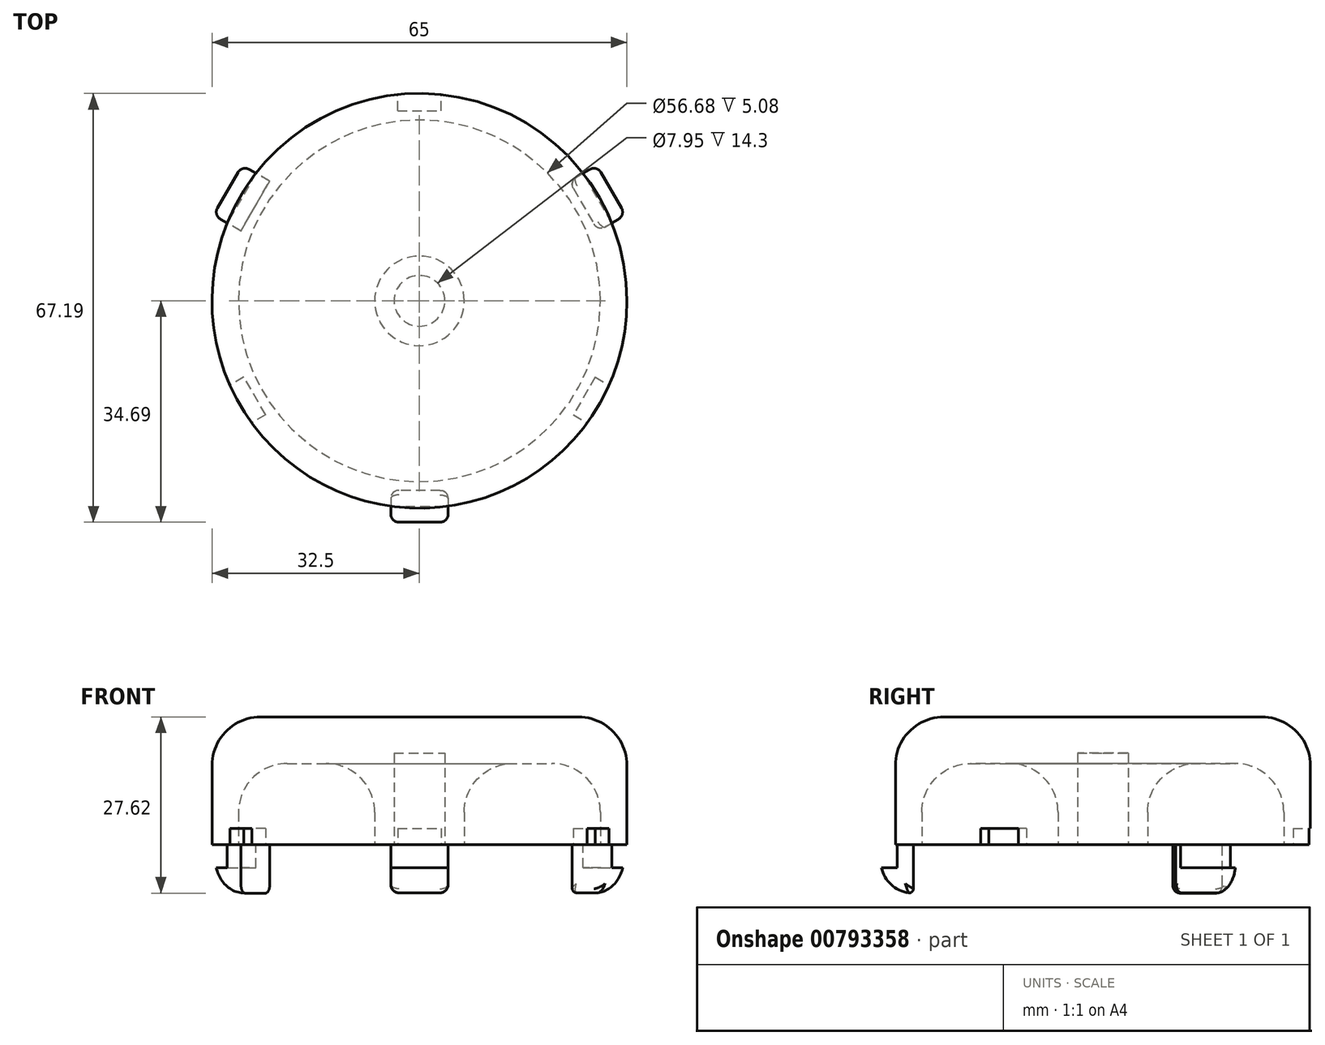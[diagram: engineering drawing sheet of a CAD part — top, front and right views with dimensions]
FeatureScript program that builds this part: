
annotation { "Feature Type Name" : "Feature", "Feature Type Description" : "" }
export const myFeature = defineFeature(function(context is Context, id is Id, definition is map)
    precondition{}
    {
        {
            var Q0;
            Q0=qCreatedBy(makeId("Top.planeOp"),FACE);
            var sketch = newSketch(context, id + "F0", { "sketchPlane" : qUnion([Q0])});
            skCircle(sketch, "E0", {"center": v(0, 0) * mm, "radius": 32.5 * mm});
            skSolve(sketch);
        }
        {
            var Q0;
            Q0=makeQuery(id+"F0.imprint","IMPRINT",FACE,{"disambiguationData":[TD([[makeQuery(id+"F0.imprint","IMPRINT",EDGE,{"derivedFrom":sQuery(id+"F0.wireOp",EDGE,"E0")}),1.0]])]});
            extrude(context, id + "F1", {"entities" : qUnion([Q0]), "depth" : 20 * mm, "offsetDistance" : 25.4 * mm});
        }
        {
            var Q0;
            Q0=makeQuery(id+"F1.opExtrude","CAP_FACE",FACE,{"disambiguationData":[OSD([sQuery(id+"F0.wireOp",EDGE,"E0")])],"isStart":false});
            fillet(context, id + "F2", {"entities" : qUnion([Q0]), "radius" : 7.62 * mm, "tangentPropagation" : true, "allowEdgeOverflow" : false});
        }
        {
            var Q0;
            Q0=makeQuery(id+"F1.opExtrude","CAP_FACE",FACE,{"disambiguationData":[OSD([sQuery(id+"F0.wireOp",EDGE,"E0")])],"isStart":true});
            var sketch = newSketch(context, id + "F3", { "sketchPlane" : qUnion([Q0])});
            skCircle(sketch, "E1", {"center": v(0, 0) * mm, "radius": 3.98 * mm});
            skSolve(sketch);
        }
        {
            var Q0;
            Q0=makeQuery(id+"F3.imprint","IMPRINT",FACE,{"disambiguationData":[TD([[makeQuery(id+"F3.imprint","IMPRINT",EDGE,{"derivedFrom":sQuery(id+"F3.wireOp",EDGE,"E1")}),1.0]])]});
            extrude(context, id + "F4", {"entities" : qUnion([Q0]), "operationType" : NewBodyOperationType.REMOVE, "oppositeDirection" : true, "depth" : 14.3 * mm, "offsetDistance" : 25.4 * mm});
        }
        {
            var Q0;
            Q0=makeQuery(id+"F1.opExtrude","CAP_FACE",FACE,{"disambiguationData":[OSD([sQuery(id+"F0.wireOp",EDGE,"E0")])],"isStart":true});
            var sketch = newSketch(context, id + "F5", { "sketchPlane" : qUnion([Q0])});
            skLineSegment(sketch, "E2.bottom", {"start": v(0, 29.69) * mm, "end": v(-4.5, 29.69) * mm});
            skLineSegment(sketch, "E2.top", {"start": v(0, 32.19) * mm, "end": v(-4.5, 32.19) * mm});
            skLineSegment(sketch, "E2.right", {"start": v(-4.5, 29.69) * mm, "end": v(-4.5, 32.19) * mm});
            skLineSegment(sketch, "E3.MirrorCS", {"start": v(0, 29.69) * mm, "end": v(4.5, 29.69) * mm});
            skLineSegment(sketch, "E4.MirrorCS", {"start": v(4.5, 29.69) * mm, "end": v(4.5, 32.19) * mm});
            skLineSegment(sketch, "E5.MirrorCS", {"start": v(0, 32.19) * mm, "end": v(4.5, 32.19) * mm});
            skLineSegment(sketch, "E6.1.0", {"start": v(-27.87, -16.1) * mm, "end": v(-30.12, -12.2) * mm});
            skLineSegment(sketch, "E6.1.1", {"start": v(-25.7, -14.84) * mm, "end": v(-27.96, -10.95) * mm});
            skLineSegment(sketch, "E6.1.2", {"start": v(-25.7, -14.84) * mm, "end": v(-23.46, -18.74) * mm});
            skLineSegment(sketch, "E6.1.3", {"start": v(-23.46, -18.74) * mm, "end": v(-25.62, -20) * mm});
            skLineSegment(sketch, "E6.1.4", {"start": v(-27.87, -16.1) * mm, "end": v(-25.62, -20) * mm});
            skLineSegment(sketch, "E6.1.5", {"start": v(-27.96, -10.95) * mm, "end": v(-30.12, -12.2) * mm});
            skLineSegment(sketch, "E6.2.0", {"start": v(27.87, -16.1) * mm, "end": v(25.62, -20) * mm});
            skLineSegment(sketch, "E6.2.1", {"start": v(25.7, -14.84) * mm, "end": v(23.46, -18.74) * mm});
            skLineSegment(sketch, "E6.2.2", {"start": v(25.7, -14.84) * mm, "end": v(27.96, -10.95) * mm});
            skLineSegment(sketch, "E6.2.3", {"start": v(27.96, -10.95) * mm, "end": v(30.12, -12.2) * mm});
            skLineSegment(sketch, "E6.2.4", {"start": v(27.87, -16.1) * mm, "end": v(30.12, -12.2) * mm});
            skLineSegment(sketch, "E6.2.5", {"start": v(23.46, -18.74) * mm, "end": v(25.62, -20) * mm});
            skPoint(sketch, "E6.center", {"position": v(0, 0) * mm});
            skSolve(sketch);
        }
        {
            var Q0;
            Q0=makeQuery(id+"F5.imprint","IMPRINT",FACE,{"disambiguationData":[TD([[makeQuery(id+"F5.imprint","IMPRINT",EDGE,{"derivedFrom":sQuery(id+"F5.wireOp",EDGE,"E2.bottom")}),-1.0]])]});
            var Q1;
            Q1=makeQuery(id+"F5.imprint","IMPRINT",FACE,{"disambiguationData":[TD([[makeQuery(id+"F5.imprint","IMPRINT",EDGE,{"derivedFrom":sQuery(id+"F5.wireOp",EDGE,"E6.2.0")}),-1.0]])]});
            var Q2;
            Q2=makeQuery(id+"F5.imprint","IMPRINT",FACE,{"disambiguationData":[TD([[makeQuery(id+"F5.imprint","IMPRINT",EDGE,{"derivedFrom":sQuery(id+"F5.wireOp",EDGE,"E6.1.0")}),-1.0]])]});
            extrude(context, id + "F6", {"entities" : qUnion([Q0, Q1, Q2]), "operationType" : NewBodyOperationType.ADD, "depth" : 7.62 * mm, "offsetDistance" : 25.4 * mm});
        }
        {
            var Q0;
            Q0=makeQuery(id+"F6.opExtrude","SWEPT_FACE",FACE,{"disambiguationData":[OSD([sQuery(id+"F5.wireOp",EDGE,"E6.1.0"),sQuery(id+"F5.wireOp",EDGE,"E6.1.4")])]});
            var sketch = newSketch(context, id + "F7", { "sketchPlane" : qUnion([Q0])});
            skLineSegment(sketch, "E7.bottom", {"start": v(4.5, -7.62) * mm, "end": v(-4.5, -7.62) * mm});
            skLineSegment(sketch, "E7.top", {"start": v(4.5, -3.62) * mm, "end": v(-4.5, -3.62) * mm});
            skLineSegment(sketch, "E7.left", {"start": v(4.5, -7.62) * mm, "end": v(4.5, -3.62) * mm});
            skLineSegment(sketch, "E7.right", {"start": v(-4.5, -7.62) * mm, "end": v(-4.5, -3.62) * mm});
            skSolve(sketch);
        }
        {
            var Q0;
            Q0=makeQuery(id+"F6.opExtrude","SWEPT_FACE",FACE,{"disambiguationData":[OSD([sQuery(id+"F5.wireOp",EDGE,"E6.2.0"),sQuery(id+"F5.wireOp",EDGE,"E6.2.4")])]});
            var sketch = newSketch(context, id + "F8", { "sketchPlane" : qUnion([Q0])});
            skLineSegment(sketch, "E8.bottom", {"start": v(4.5, -7.62) * mm, "end": v(-4.5, -7.62) * mm});
            skLineSegment(sketch, "E8.top", {"start": v(4.5, -3.62) * mm, "end": v(-4.5, -3.62) * mm});
            skLineSegment(sketch, "E8.left", {"start": v(4.5, -7.62) * mm, "end": v(4.5, -3.62) * mm});
            skLineSegment(sketch, "E8.right", {"start": v(-4.5, -7.62) * mm, "end": v(-4.5, -3.62) * mm});
            skSolve(sketch);
        }
        {
            var Q0;
            Q0=makeQuery(id+"F6.opExtrude","SWEPT_FACE",FACE,{"disambiguationData":[OSD([sQuery(id+"F5.wireOp",EDGE,"E2.top"),sQuery(id+"F5.wireOp",EDGE,"E5.MirrorCS")])]});
            var sketch = newSketch(context, id + "F9", { "sketchPlane" : qUnion([Q0])});
            skLineSegment(sketch, "E9.bottom", {"start": v(-4.5, -7.62) * mm, "end": v(4.5, -7.62) * mm});
            skLineSegment(sketch, "E9.top", {"start": v(-4.5, -3.62) * mm, "end": v(4.5, -3.62) * mm});
            skLineSegment(sketch, "E9.left", {"start": v(-4.5, -7.62) * mm, "end": v(-4.5, -3.62) * mm});
            skLineSegment(sketch, "E9.right", {"start": v(4.5, -7.62) * mm, "end": v(4.5, -3.62) * mm});
            skSolve(sketch);
        }
        {
            var Q0;
            Q0=makeQuery(id+"F9.imprint","IMPRINT",FACE,{"disambiguationData":[TD([[makeQuery(id+"F9.imprint","IMPRINT",EDGE,{"derivedFrom":sQuery(id+"F9.wireOp",EDGE,"E9.bottom")}),1.0]])]});
            extrude(context, id + "F10", {"entities" : qUnion([Q0]), "operationType" : NewBodyOperationType.ADD, "depth" : 2.5 * mm, "offsetDistance" : 25.4 * mm});
        }
        {
            var Q0;
            Q0=makeQuery(id+"F7.imprint","IMPRINT",FACE,{"disambiguationData":[TD([[makeQuery(id+"F7.imprint","IMPRINT",EDGE,{"derivedFrom":sQuery(id+"F7.wireOp",EDGE,"E7.bottom")}),1.0]])]});
            extrude(context, id + "F11", {"entities" : qUnion([Q0]), "operationType" : NewBodyOperationType.ADD, "depth" : 2.5 * mm, "offsetDistance" : 25.4 * mm});
        }
        {
            var Q0;
            Q0=makeQuery(id+"F8.imprint","IMPRINT",FACE,{"disambiguationData":[TD([[makeQuery(id+"F8.imprint","IMPRINT",EDGE,{"derivedFrom":sQuery(id+"F8.wireOp",EDGE,"E8.bottom")}),1.0]])]});
            extrude(context, id + "F12", {"entities" : qUnion([Q0]), "operationType" : NewBodyOperationType.ADD, "depth" : 2.5 * mm, "offsetDistance" : 25.4 * mm});
        }
        {
            var Q0;
            Q0=makeQuery(id+"F12.opExtrude","CAP_EDGE",EDGE,{"disambiguationData":[OSD([sQuery(id+"F8.wireOp",EDGE,"E8.bottom")])],"isStart":false});
            var Q1;
            Q1=makeQuery(id+"F10.opExtrude","CAP_EDGE",EDGE,{"disambiguationData":[OSD([sQuery(id+"F9.wireOp",EDGE,"E9.bottom")])],"isStart":false});
            var Q2;
            Q2=makeQuery(id+"F11.opExtrude","CAP_EDGE",EDGE,{"disambiguationData":[OSD([sQuery(id+"F7.wireOp",EDGE,"E7.bottom")])],"isStart":false});
            fillet(context, id + "F13", {"entities" : qUnion([Q0, Q1, Q2]), "radius" : 5.08 * mm, "tangentPropagation" : true, "allowEdgeOverflow" : false});
        }
        {
            var Q0;
            Q0=makeQuery(id+"F6.opExtrude","CAP_EDGE",EDGE,{"disambiguationData":[OSD([sQuery(id+"F5.wireOp",EDGE,"E2.bottom"),sQuery(id+"F5.wireOp",EDGE,"E3.MirrorCS")])],"isStart":false});
            var Q1;
            {var subQ0=sQuery(id+"F7.wireOp",EDGE,"E7.bottom");Q1=makeQuery(id+"F13.opFillet","BLEND_EDGE",EDGE,{"blendedFrom":[makeQuery(id+"F11.opExtrude","CAP_EDGE",EDGE,{"disambiguationData":[OSD([subQ0])],"isStart":false}),makeQuery(id+"F11.boolean.opBoolean","MERGE",FACE,{"derivedFrom":[makeQuery(id+"F6.opExtrude","CAP_FACE",FACE,{"disambiguationData":[OSD([sQuery(id+"F5.wireOp",EDGE,"E6.1.0"),sQuery(id+"F5.wireOp",EDGE,"E6.1.1"),sQuery(id+"F5.wireOp",EDGE,"E6.1.2"),sQuery(id+"F5.wireOp",EDGE,"E6.1.3"),sQuery(id+"F5.wireOp",EDGE,"E6.1.4"),sQuery(id+"F5.wireOp",EDGE,"E6.1.5")])],"isStart":false}),makeQuery(id+"F11.opExtrude","SWEPT_FACE",FACE,{"disambiguationData":[OSD([subQ0])]})]})],"blendedInto":[makeQuery(id+"F11.boolean.opBoolean","MERGE",FACE,{"derivedFrom":[makeQuery(id+"F6.opExtrude","CAP_FACE",FACE,{"disambiguationData":[OSD([sQuery(id+"F5.wireOp",EDGE,"E6.1.0"),sQuery(id+"F5.wireOp",EDGE,"E6.1.1"),sQuery(id+"F5.wireOp",EDGE,"E6.1.2"),sQuery(id+"F5.wireOp",EDGE,"E6.1.3"),sQuery(id+"F5.wireOp",EDGE,"E6.1.4"),sQuery(id+"F5.wireOp",EDGE,"E6.1.5")])],"isStart":false}),makeQuery(id+"F11.opExtrude","SWEPT_FACE",FACE,{"disambiguationData":[OSD([subQ0])]})]})]});}
            var Q2;
            Q2=makeQuery(id+"F6.opExtrude","CAP_EDGE",EDGE,{"disambiguationData":[OSD([sQuery(id+"F5.wireOp",EDGE,"E6.2.1"),sQuery(id+"F5.wireOp",EDGE,"E6.2.2")])],"isStart":false});
            fillet(context, id + "F14", {"entities" : qUnion([Q0, Q1, Q2]), "radius" : 0.64 * mm, "tangentPropagation" : true, "allowEdgeOverflow" : false});
        }
        {
            var Q0;
            Q0=makeQuery(id+"F13.opFillet","BLEND_EDGE",EDGE,{"blendedFrom":[makeQuery(id+"F11.opExtrude","CAP_EDGE",EDGE,{"disambiguationData":[OSD([sQuery(id+"F7.wireOp",EDGE,"E7.bottom")])],"isStart":false}),makeQuery(id+"F11.boolean.opBoolean","MERGE",FACE,{"derivedFrom":[makeQuery(id+"F6.opExtrude","SWEPT_FACE",FACE,{"disambiguationData":[OSD([sQuery(id+"F5.wireOp",EDGE,"E6.1.3")])]}),makeQuery(id+"F11.opExtrude","SWEPT_FACE",FACE,{"disambiguationData":[OSD([sQuery(id+"F7.wireOp",EDGE,"E7.right")])]})]})],"blendedInto":[makeQuery(id+"F11.boolean.opBoolean","MERGE",FACE,{"derivedFrom":[makeQuery(id+"F6.opExtrude","SWEPT_FACE",FACE,{"disambiguationData":[OSD([sQuery(id+"F5.wireOp",EDGE,"E6.1.3")])]}),makeQuery(id+"F11.opExtrude","SWEPT_FACE",FACE,{"disambiguationData":[OSD([sQuery(id+"F7.wireOp",EDGE,"E7.right")])]})]})]});
            var Q1;
            Q1=makeQuery(id+"F13.opFillet","BLEND_EDGE",EDGE,{"blendedFrom":[makeQuery(id+"F11.opExtrude","CAP_EDGE",EDGE,{"disambiguationData":[OSD([sQuery(id+"F7.wireOp",EDGE,"E7.bottom")])],"isStart":false}),makeQuery(id+"F11.boolean.opBoolean","MERGE",FACE,{"derivedFrom":[makeQuery(id+"F6.opExtrude","SWEPT_FACE",FACE,{"disambiguationData":[OSD([sQuery(id+"F5.wireOp",EDGE,"E6.1.5")])]}),makeQuery(id+"F11.opExtrude","SWEPT_FACE",FACE,{"disambiguationData":[OSD([sQuery(id+"F7.wireOp",EDGE,"E7.left")])]})]})],"blendedInto":[makeQuery(id+"F11.boolean.opBoolean","MERGE",FACE,{"derivedFrom":[makeQuery(id+"F6.opExtrude","SWEPT_FACE",FACE,{"disambiguationData":[OSD([sQuery(id+"F5.wireOp",EDGE,"E6.1.5")])]}),makeQuery(id+"F11.opExtrude","SWEPT_FACE",FACE,{"disambiguationData":[OSD([sQuery(id+"F7.wireOp",EDGE,"E7.left")])]})]})]});
            var Q2;
            Q2=makeQuery(id+"F13.opFillet","BLEND_EDGE",EDGE,{"blendedFrom":[makeQuery(id+"F10.opExtrude","CAP_EDGE",EDGE,{"disambiguationData":[OSD([sQuery(id+"F9.wireOp",EDGE,"E9.bottom")])],"isStart":false}),makeQuery(id+"F10.boolean.opBoolean","MERGE",FACE,{"derivedFrom":[makeQuery(id+"F6.opExtrude","SWEPT_FACE",FACE,{"disambiguationData":[OSD([sQuery(id+"F5.wireOp",EDGE,"E2.right")])]}),makeQuery(id+"F10.opExtrude","SWEPT_FACE",FACE,{"disambiguationData":[OSD([sQuery(id+"F9.wireOp",EDGE,"E9.left")])]})]})],"blendedInto":[makeQuery(id+"F10.boolean.opBoolean","MERGE",FACE,{"derivedFrom":[makeQuery(id+"F6.opExtrude","SWEPT_FACE",FACE,{"disambiguationData":[OSD([sQuery(id+"F5.wireOp",EDGE,"E2.right")])]}),makeQuery(id+"F10.opExtrude","SWEPT_FACE",FACE,{"disambiguationData":[OSD([sQuery(id+"F9.wireOp",EDGE,"E9.left")])]})]})]});
            var Q3;
            Q3=makeQuery(id+"F13.opFillet","BLEND_EDGE",EDGE,{"blendedFrom":[makeQuery(id+"F12.opExtrude","CAP_EDGE",EDGE,{"disambiguationData":[OSD([sQuery(id+"F8.wireOp",EDGE,"E8.bottom")])],"isStart":false}),makeQuery(id+"F12.boolean.opBoolean","MERGE",FACE,{"derivedFrom":[makeQuery(id+"F6.opExtrude","SWEPT_FACE",FACE,{"disambiguationData":[OSD([sQuery(id+"F5.wireOp",EDGE,"E6.2.5")])]}),makeQuery(id+"F12.opExtrude","SWEPT_FACE",FACE,{"disambiguationData":[OSD([sQuery(id+"F8.wireOp",EDGE,"E8.left")])]})]})],"blendedInto":[makeQuery(id+"F12.boolean.opBoolean","MERGE",FACE,{"derivedFrom":[makeQuery(id+"F6.opExtrude","SWEPT_FACE",FACE,{"disambiguationData":[OSD([sQuery(id+"F5.wireOp",EDGE,"E6.2.5")])]}),makeQuery(id+"F12.opExtrude","SWEPT_FACE",FACE,{"disambiguationData":[OSD([sQuery(id+"F8.wireOp",EDGE,"E8.left")])]})]})]});
            var Q4;
            Q4=makeQuery(id+"F13.opFillet","BLEND_EDGE",EDGE,{"blendedFrom":[makeQuery(id+"F12.opExtrude","CAP_EDGE",EDGE,{"disambiguationData":[OSD([sQuery(id+"F8.wireOp",EDGE,"E8.bottom")])],"isStart":false}),makeQuery(id+"F12.boolean.opBoolean","MERGE",FACE,{"derivedFrom":[makeQuery(id+"F6.opExtrude","SWEPT_FACE",FACE,{"disambiguationData":[OSD([sQuery(id+"F5.wireOp",EDGE,"E6.2.3")])]}),makeQuery(id+"F12.opExtrude","SWEPT_FACE",FACE,{"disambiguationData":[OSD([sQuery(id+"F8.wireOp",EDGE,"E8.right")])]})]})],"blendedInto":[makeQuery(id+"F12.boolean.opBoolean","MERGE",FACE,{"derivedFrom":[makeQuery(id+"F6.opExtrude","SWEPT_FACE",FACE,{"disambiguationData":[OSD([sQuery(id+"F5.wireOp",EDGE,"E6.2.3")])]}),makeQuery(id+"F12.opExtrude","SWEPT_FACE",FACE,{"disambiguationData":[OSD([sQuery(id+"F8.wireOp",EDGE,"E8.right")])]})]})]});
            var Q5;
            Q5=makeQuery(id+"F13.opFillet","BLEND_EDGE",EDGE,{"blendedFrom":[makeQuery(id+"F10.opExtrude","CAP_EDGE",EDGE,{"disambiguationData":[OSD([sQuery(id+"F9.wireOp",EDGE,"E9.bottom")])],"isStart":false}),makeQuery(id+"F10.boolean.opBoolean","MERGE",FACE,{"derivedFrom":[makeQuery(id+"F6.opExtrude","SWEPT_FACE",FACE,{"disambiguationData":[OSD([sQuery(id+"F5.wireOp",EDGE,"E4.MirrorCS")])]}),makeQuery(id+"F10.opExtrude","SWEPT_FACE",FACE,{"disambiguationData":[OSD([sQuery(id+"F9.wireOp",EDGE,"E9.right")])]})]})],"blendedInto":[makeQuery(id+"F10.boolean.opBoolean","MERGE",FACE,{"derivedFrom":[makeQuery(id+"F6.opExtrude","SWEPT_FACE",FACE,{"disambiguationData":[OSD([sQuery(id+"F5.wireOp",EDGE,"E4.MirrorCS")])]}),makeQuery(id+"F10.opExtrude","SWEPT_FACE",FACE,{"disambiguationData":[OSD([sQuery(id+"F9.wireOp",EDGE,"E9.right")])]})]})]});
            fillet(context, id + "F15", {"entities" : qUnion([Q0, Q1, Q2, Q3, Q4, Q5]), "radius" : 1.27 * mm, "tangentPropagation" : true, "allowEdgeOverflow" : false});
        }
        {
            var Q0;
            {var subQ0=sQuery(id+"F0.wireOp",EDGE,"E0");var subQ1=makeQuery(id+"F1.opExtrude","CAP_FACE",FACE,{"disambiguationData":[OSD([subQ0])],"isStart":true});Q0=makeQuery(id+"F6.boolean.opBoolean","SPLIT",FACE,{"disambiguationData":[TD([makeQuery(id+"F1.opExtrude","SWEPT_FACE",FACE,{"disambiguationData":[OSD([subQ0])]}),subQ1,makeQuery(id+"F4.boolean.opBoolean","COPY",FACE,{"derivedFrom":makeQuery(id+"F4.opExtrude","SWEPT_FACE",FACE,{"disambiguationData":[OSD([sQuery(id+"F3.wireOp",EDGE,"E1")])]})}),makeQuery(id+"F6.opExtrude","SWEPT_FACE",FACE,{"disambiguationData":[OSD([sQuery(id+"F5.wireOp",EDGE,"E2.bottom"),sQuery(id+"F5.wireOp",EDGE,"E3.MirrorCS")])]}),makeQuery(id+"F6.opExtrude","SWEPT_FACE",FACE,{"disambiguationData":[OSD([sQuery(id+"F5.wireOp",EDGE,"E2.top"),sQuery(id+"F5.wireOp",EDGE,"E5.MirrorCS")])]}),makeQuery(id+"F6.opExtrude","SWEPT_FACE",FACE,{"disambiguationData":[OSD([sQuery(id+"F5.wireOp",EDGE,"E2.right")])]}),makeQuery(id+"F6.opExtrude","SWEPT_FACE",FACE,{"disambiguationData":[OSD([sQuery(id+"F5.wireOp",EDGE,"E4.MirrorCS")])]}),makeQuery(id+"F6.opExtrude","SWEPT_FACE",FACE,{"disambiguationData":[OSD([sQuery(id+"F5.wireOp",EDGE,"E6.1.0"),sQuery(id+"F5.wireOp",EDGE,"E6.1.4")])]}),makeQuery(id+"F6.opExtrude","SWEPT_FACE",FACE,{"disambiguationData":[OSD([sQuery(id+"F5.wireOp",EDGE,"E6.1.1"),sQuery(id+"F5.wireOp",EDGE,"E6.1.2")])]}),makeQuery(id+"F6.opExtrude","SWEPT_FACE",FACE,{"disambiguationData":[OSD([sQuery(id+"F5.wireOp",EDGE,"E6.1.3")])]}),makeQuery(id+"F6.opExtrude","SWEPT_FACE",FACE,{"disambiguationData":[OSD([sQuery(id+"F5.wireOp",EDGE,"E6.1.5")])]}),makeQuery(id+"F6.opExtrude","SWEPT_FACE",FACE,{"disambiguationData":[OSD([sQuery(id+"F5.wireOp",EDGE,"E6.2.0"),sQuery(id+"F5.wireOp",EDGE,"E6.2.4")])]}),makeQuery(id+"F6.opExtrude","SWEPT_FACE",FACE,{"disambiguationData":[OSD([sQuery(id+"F5.wireOp",EDGE,"E6.2.1"),sQuery(id+"F5.wireOp",EDGE,"E6.2.2")])]}),makeQuery(id+"F6.opExtrude","SWEPT_FACE",FACE,{"disambiguationData":[OSD([sQuery(id+"F5.wireOp",EDGE,"E6.2.3")])]}),makeQuery(id+"F6.opExtrude","SWEPT_FACE",FACE,{"disambiguationData":[OSD([sQuery(id+"F5.wireOp",EDGE,"E6.2.5")])]})])],"derivedFrom":subQ1});}
            var sketch = newSketch(context, id + "F16", { "sketchPlane" : qUnion([Q0])});
            skCircle(sketch, "E10", {"center": v(0, 0) * mm, "radius": 7.02 * mm});
            skCircle(sketch, "E11", {"center": v(0, 0) * mm, "radius": 28.34 * mm});
            skSolve(sketch);
        }
        {
            var Q0;
            Q0=makeQuery(id+"F16.imprint","IMPRINT",FACE,{"disambiguationData":[TD([[makeQuery(id+"F16.imprint","IMPRINT",EDGE,{"derivedFrom":sQuery(id+"F16.wireOp",EDGE,"E10")}),-1.0]])]});
            extrude(context, id + "F17", {"entities" : qUnion([Q0]), "operationType" : NewBodyOperationType.REMOVE, "oppositeDirection" : true, "depth" : 12.7 * mm, "offsetDistance" : 25.4 * mm});
        }
        {
            var Q0;
            Q0=makeQuery(id+"F17.boolean.opBoolean","COPY",EDGE,{"derivedFrom":makeQuery(id+"F17.opExtrude","CAP_EDGE",EDGE,{"disambiguationData":[OSD([sQuery(id+"F16.wireOp",EDGE,"E11")])],"isStart":false})});
            var Q1;
            Q1=makeQuery(id+"F17.boolean.opBoolean","COPY",EDGE,{"derivedFrom":makeQuery(id+"F17.opExtrude","CAP_EDGE",EDGE,{"disambiguationData":[OSD([sQuery(id+"F16.wireOp",EDGE,"E10")])],"isStart":false})});
            fillet(context, id + "F18", {"entities" : qUnion([Q0, Q1]), "radius" : 7.62 * mm, "tangentPropagation" : true, "allowEdgeOverflow" : false});
        }
        {
            var Q0;
            {var subQ0=sQuery(id+"F5.wireOp",EDGE,"E6.2.3");var subQ1=makeQuery(id+"F6.opExtrude","SWEPT_FACE",FACE,{"disambiguationData":[OSD([subQ0])]});var subQ2=sQuery(id+"F5.wireOp",EDGE,"E6.2.5");var subQ3=makeQuery(id+"F6.opExtrude","SWEPT_FACE",FACE,{"disambiguationData":[OSD([subQ2])]});var subQ4=sQuery(id+"F5.wireOp",EDGE,"E6.2.2");var subQ5=sQuery(id+"F5.wireOp",EDGE,"E6.2.1");var subQ6=makeQuery(id+"F6.opExtrude","SWEPT_FACE",FACE,{"disambiguationData":[OSD([subQ5,subQ4])]});var subQ7=makeQuery(id+"F6.opExtrude","SWEPT_FACE",FACE,{"disambiguationData":[OSD([sQuery(id+"F5.wireOp",EDGE,"E6.2.0"),sQuery(id+"F5.wireOp",EDGE,"E6.2.4")])]});var subQ8=makeQuery(id+"F6.opExtrude","SWEPT_FACE",FACE,{"disambiguationData":[OSD([sQuery(id+"F5.wireOp",EDGE,"E2.top"),sQuery(id+"F5.wireOp",EDGE,"E5.MirrorCS")])]});var subQ9=sQuery(id+"F0.wireOp",EDGE,"E0");var subQ10=makeQuery(id+"F1.opExtrude","CAP_FACE",FACE,{"disambiguationData":[OSD([subQ9])],"isStart":true});var subQ11=sQuery(id+"F5.wireOp",EDGE,"E3.MirrorCS");var subQ12=sQuery(id+"F5.wireOp",EDGE,"E2.bottom");var subQ13=makeQuery(id+"F6.opExtrude","SWEPT_FACE",FACE,{"disambiguationData":[OSD([subQ12,subQ11])]});var subQ14=makeQuery(id+"F1.opExtrude","SWEPT_FACE",FACE,{"disambiguationData":[OSD([subQ9])]});var subQ15=sQuery(id+"F5.wireOp",EDGE,"E2.right");var subQ16=makeQuery(id+"F6.opExtrude","SWEPT_FACE",FACE,{"disambiguationData":[OSD([subQ15])]});var subQ17=sQuery(id+"F5.wireOp",EDGE,"E4.MirrorCS");var subQ18=makeQuery(id+"F6.opExtrude","SWEPT_FACE",FACE,{"disambiguationData":[OSD([subQ17])]});var subQ19=makeQuery(id+"F6.opExtrude","SWEPT_FACE",FACE,{"disambiguationData":[OSD([sQuery(id+"F5.wireOp",EDGE,"E6.1.0"),sQuery(id+"F5.wireOp",EDGE,"E6.1.4")])]});var subQ20=makeQuery(id+"F6.opExtrude","SWEPT_FACE",FACE,{"disambiguationData":[OSD([sQuery(id+"F5.wireOp",EDGE,"E6.1.1"),sQuery(id+"F5.wireOp",EDGE,"E6.1.2")])]});var subQ21=makeQuery(id+"F6.opExtrude","SWEPT_FACE",FACE,{"disambiguationData":[OSD([sQuery(id+"F5.wireOp",EDGE,"E6.1.3")])]});var subQ22=makeQuery(id+"F6.opExtrude","SWEPT_FACE",FACE,{"disambiguationData":[OSD([sQuery(id+"F5.wireOp",EDGE,"E6.1.5")])]});Q0=makeQuery(id+"F17.boolean.opBoolean","SPLIT",FACE,{"disambiguationData":[TD([subQ14])],"derivedFrom":makeQuery(id+"F6.boolean.opBoolean","SPLIT",FACE,{"disambiguationData":[TD([subQ14,subQ10,makeQuery(id+"F4.boolean.opBoolean","COPY",FACE,{"derivedFrom":makeQuery(id+"F4.opExtrude","SWEPT_FACE",FACE,{"disambiguationData":[OSD([sQuery(id+"F3.wireOp",EDGE,"E1")])]})}),subQ13,subQ8,subQ16,subQ18,subQ19,subQ20,subQ21,subQ22,subQ7,subQ6,subQ1,subQ3])],"derivedFrom":subQ10})});}
            var sketch = newSketch(context, id + "F19", { "sketchPlane" : qUnion([Q0])});
            skLineSegment(sketch, "E12.bottom", {"start": v(-3.42, -29.8) * mm, "end": v(3.42, -29.8) * mm});
            skLineSegment(sketch, "E12.top", {"start": v(-3.42, -35.2) * mm, "end": v(3.42, -35.2) * mm});
            skLineSegment(sketch, "E12.left", {"start": v(-3.42, -29.8) * mm, "end": v(-3.42, -35.2) * mm});
            skLineSegment(sketch, "E12.right", {"start": v(3.42, -29.8) * mm, "end": v(3.42, -35.2) * mm});
            skPoint(sketch, "E12.middle", {"position": v(0, -32.5) * mm});
            skLineSegment(sketch, "E13.1.0", {"start": v(32.2, 14.64) * mm, "end": v(28.78, 20.56) * mm});
            skLineSegment(sketch, "E13.1.1", {"start": v(27.52, 11.94) * mm, "end": v(32.2, 14.64) * mm});
            skLineSegment(sketch, "E13.1.2", {"start": v(27.52, 11.94) * mm, "end": v(24.1, 17.86) * mm});
            skLineSegment(sketch, "E13.1.3", {"start": v(24.1, 17.86) * mm, "end": v(28.78, 20.56) * mm});
            skLineSegment(sketch, "E13.2.0", {"start": v(-28.78, 20.56) * mm, "end": v(-32.2, 14.64) * mm});
            skLineSegment(sketch, "E13.2.1", {"start": v(-24.1, 17.86) * mm, "end": v(-28.78, 20.56) * mm});
            skLineSegment(sketch, "E13.2.2", {"start": v(-24.1, 17.86) * mm, "end": v(-27.52, 11.94) * mm});
            skLineSegment(sketch, "E13.2.3", {"start": v(-27.52, 11.94) * mm, "end": v(-32.2, 14.64) * mm});
            skPoint(sketch, "E13.center", {"position": v(0, 0) * mm});
            skSolve(sketch);
        }
        {
            var Q0;
            {var subQ0=sQuery(id+"F19.wireOp",EDGE,"E12.top");Q0=makeQuery(id+"F19.imprint","IMPRINT",FACE,{"disambiguationData":[TD([[makeQuery(id+"F19.imprint","IMPRINT",EDGE,{"derivedFrom":subQ0}),1.0]])]});}
            var Q1;
            {var subQ0=sQuery(id+"F19.wireOp",EDGE,"E12.bottom");Q1=makeQuery(id+"F19.imprint","IMPRINT",FACE,{"disambiguationData":[TD([[makeQuery(id+"F19.imprint","IMPRINT",EDGE,{"derivedFrom":subQ0}),-1.0]])]});}
            var Q2;
            {var subQ0=sQuery(id+"F19.wireOp",EDGE,"E13.2.0");Q2=makeQuery(id+"F19.imprint","IMPRINT",FACE,{"disambiguationData":[TD([[makeQuery(id+"F19.imprint","IMPRINT",EDGE,{"derivedFrom":subQ0}),1.0]])]});}
            var Q3;
            {var subQ0=sQuery(id+"F19.wireOp",EDGE,"E13.2.2");Q3=makeQuery(id+"F19.imprint","IMPRINT",FACE,{"disambiguationData":[TD([[makeQuery(id+"F19.imprint","IMPRINT",EDGE,{"derivedFrom":subQ0}),-1.0]])]});}
            var Q4;
            {var subQ0=sQuery(id+"F19.wireOp",EDGE,"E13.1.0");Q4=makeQuery(id+"F19.imprint","IMPRINT",FACE,{"disambiguationData":[TD([[makeQuery(id+"F19.imprint","IMPRINT",EDGE,{"derivedFrom":subQ0}),1.0]])]});}
            var Q5;
            {var subQ0=sQuery(id+"F19.wireOp",EDGE,"E13.1.2");Q5=makeQuery(id+"F19.imprint","IMPRINT",FACE,{"disambiguationData":[TD([[makeQuery(id+"F19.imprint","IMPRINT",EDGE,{"derivedFrom":subQ0}),-1.0]])]});}
            extrude(context, id + "F20", {"entities" : qUnion([Q0, Q1, Q2, Q3, Q4, Q5]), "operationType" : NewBodyOperationType.REMOVE, "oppositeDirection" : true, "depth" : 2.54 * mm, "offsetDistance" : 25.4 * mm});
        }
    });
